# Revit family: Haworth_Immerse_SingleTable_Round_EU_PRELIMINARY
name_source: partatom
category: Furniture Systems
revit_build: Autodesk Revit 2018 (Build: 20170223_1515(x64)
units: mm (PartAtom-declared; Revit-internal decimal feet)

## family parameters
Always vertical = Yes
Cut with Voids When Loaded = No
OmniClass Number = 23.40.70.14.64.21
OmniClass Title = Systems Furniture
Part Type = Normal
Room Calculation Point = No
Round Connector Dimension = Use Diameter
Shared = No
Work Plane-Based = No

## types (9) — shared parameters
Assembly Code = E2020200
Cable Finish = Haworth _ Polymer _ Undecided
Cable Snake = Yes
Description = Haworth - Immerse - Single Desk - Circular
Manufacturer = Haworth
Model = IMSICI1X1X
Revision Number = 1
Round Planter = Yes
Round Planter Void Height = 61 cm
Size = Verify Final Dim w/ Haworth
Standard Diameter = 120, 150, 160 cm
Standard Height = 74, 91.5, 99 cm
URL = https://www.haworth.com
URL - Product = https://www.haworth.com
Understructure Inset = 40 cm
Understucture Thickness = 4 cm
Void Baseline Height = 46 cm
Void Diameter = 45 cm
Warranty = http://www.haworth.com

## per-type parameters (varying)
| type | Actual Depth | Actual Height | Blend Bottom Diameter | Cable Height | High Table | Large | Low Table | Medium | Medium Table | Small | Understuctuer Bottom |
| 120dia x 91.5h - Round Planter | 120 cm | 92 cm | 110 cm | 29 cm | No | No | No | No | Yes | Yes | 85 cm |
| 120dia x 74h - Round Planter | 120 cm | 74 cm | 110 cm | 11 cm | No | No | Yes | No | No | Yes | 68 cm |
| 120dia x 99h - Round Planter | 120 cm | 99 cm | 110 cm | 36 cm | Yes | No | No | No | No | Yes | 93 cm |
| 150dia x 74h - Round Planter | 150 cm | 74 cm | 140 cm | 11 cm | No | No | Yes | Yes | No | No | 68 cm |
| 150dia x 91.5h - Round Planter | 150 cm | 92 cm | 140 cm | 29 cm | No | No | No | Yes | Yes | No | 85 cm |
| 150dia x 99h - Round Planter | 150 cm | 99 cm | 140 cm | 36 cm | Yes | No | No | Yes | No | No | 93 cm |
| 160dia x 74h - Round Planter | 160 cm | 74 cm | 150 cm | 11 cm | No | Yes | Yes | No | No | No | 68 cm |
| 160dia x 91.5h - Round Planter | 160 cm | 92 cm | 150 cm | 29 cm | No | Yes | No | No | Yes | No | 85 cm |
| 160dia x 99h - Round Planter | 160 cm | 99 cm | 150 cm | 36 cm | Yes | Yes | No | No | No | No | 93 cm |

## geometry (parser evidence)
native form markers: Blend x2, Sweep x12
no freeform markers — native parametric forms only
